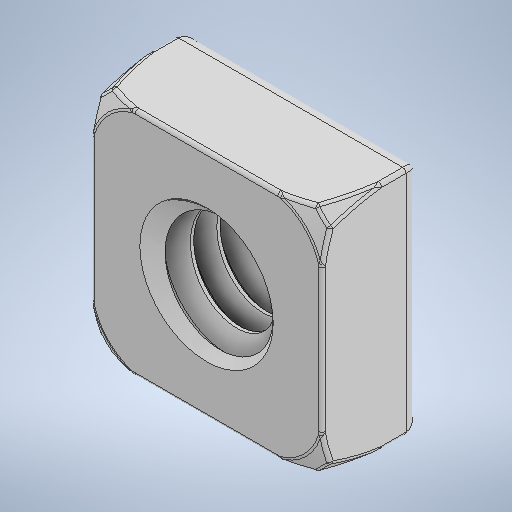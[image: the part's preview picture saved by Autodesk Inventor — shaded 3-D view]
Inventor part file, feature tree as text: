
AUTODESK INVENTOR PART (.ipt)
format: ipt  version: 2025 (Build 290162000, 162)  size: 515,584 bytes
history: native  units: mm
features: mirror x1
ambient origin geometry x8: Origin, YZ Plane, XZ Plane, XY Plane, X Axis, Y Axis, Z Axis, Center Point
bodies: Solid1 (feature_tree)
feature tree (1):
  mirror  "Mirror1"
